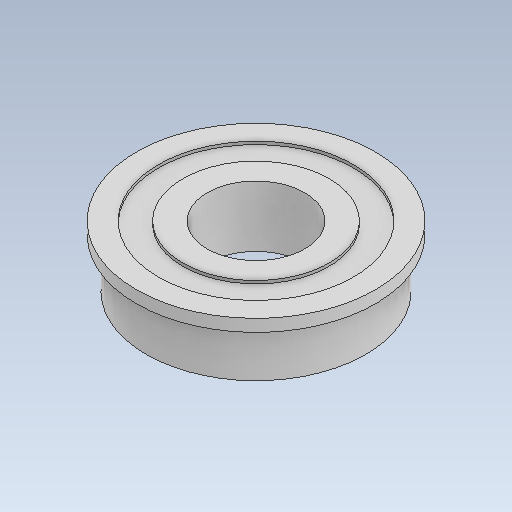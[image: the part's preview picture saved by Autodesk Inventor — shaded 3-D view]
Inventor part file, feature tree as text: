
AUTODESK INVENTOR PART (.ipt)
format: ipt  version: 2020 (Build 240168000, 168)  size: 130,048 bytes
history: native  units: in
note: dims shown in document units (in); Inventor stores cm internally (conversion verified against a paired STEP export)
features: revolve x1
ambient origin geometry x8: Origin, YZ Plane, XZ Plane, XY Plane, X Axis, Y Axis, Z Axis, Center Point
bodies: Solid1 (feature_tree)
feature tree (1):
  revolve  "Revolve1"  [1 undecoded]
note: 1 required parameter value undecoded (feature->parameter linkage not recoverable at this tier; creation-order binding heuristic only, values carry confidence <= 0.55)
